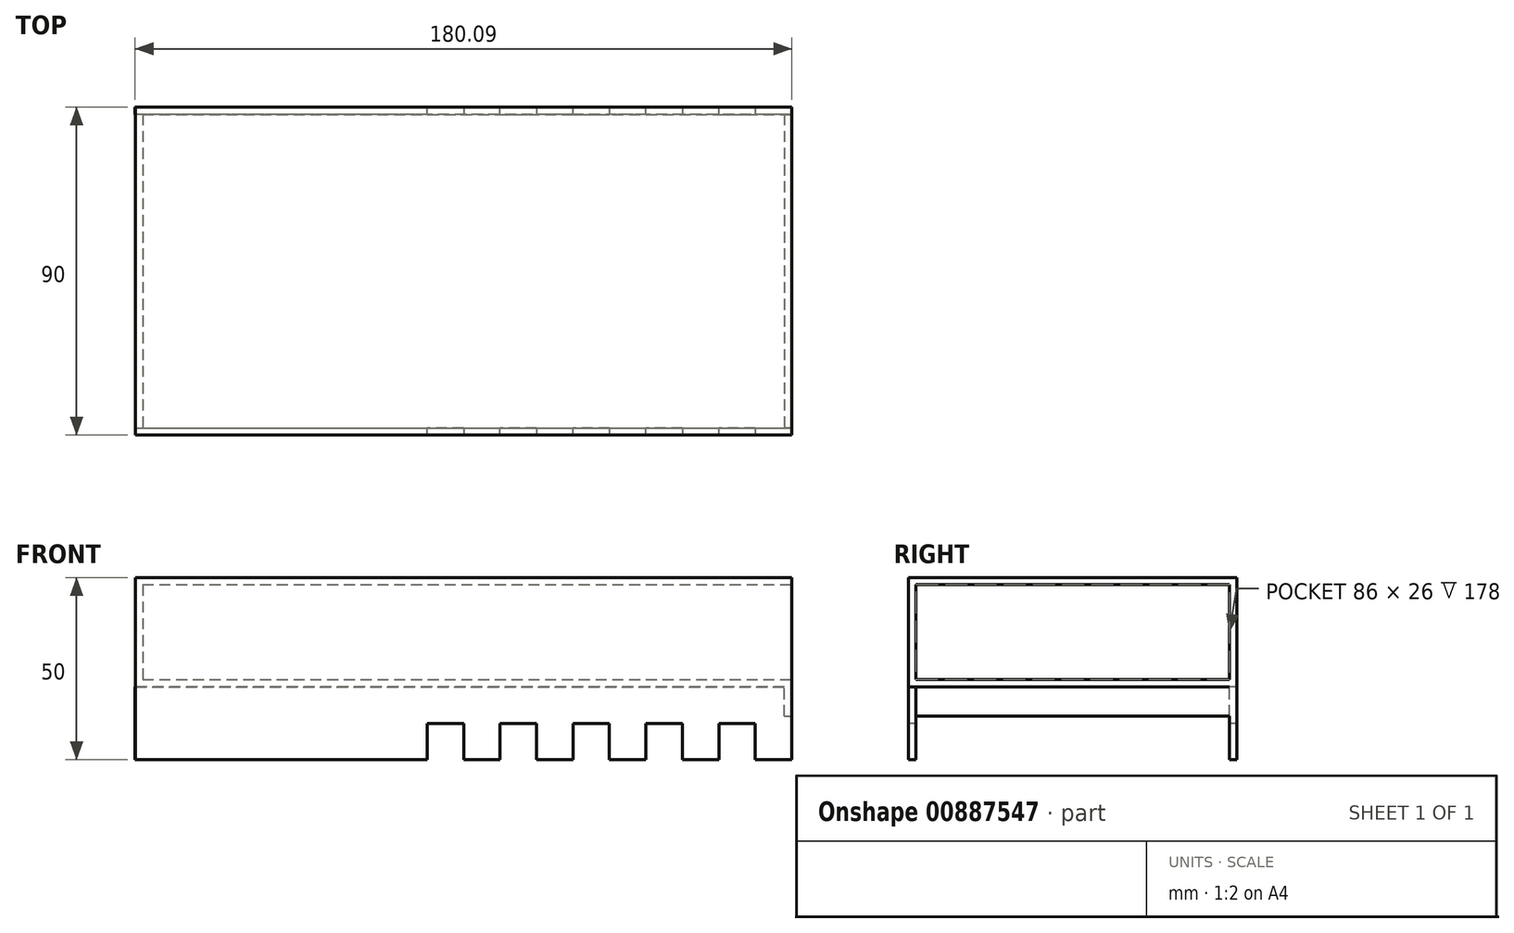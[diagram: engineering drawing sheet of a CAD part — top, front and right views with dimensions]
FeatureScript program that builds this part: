
annotation { "Feature Type Name" : "Feature", "Feature Type Description" : "" }
export const myFeature = defineFeature(function(context is Context, id is Id, definition is map)
    precondition{}
    {
        {
            var Q0;
            Q0=qCreatedBy(makeId("Top.planeOp"),FACE);
            var sketch = newSketch(context, id + "F0", { "sketchPlane" : qUnion([Q0])});
            skLineSegment(sketch, "E0.bottom", {"start": v(-90, 45) * mm, "end": v(90, 45) * mm});
            skLineSegment(sketch, "E0.top", {"start": v(-90, -45) * mm, "end": v(90, -45) * mm});
            skLineSegment(sketch, "E0.left", {"start": v(-90, 45) * mm, "end": v(-90, -45) * mm});
            skLineSegment(sketch, "E0.right", {"start": v(90, 45) * mm, "end": v(90, -45) * mm});
            skPoint(sketch, "E0.middle", {"position": v(0, 0) * mm});
            skSolve(sketch);
        }
        {
            var Q0;
            Q0=makeQuery(id+"F0.imprint","IMPRINT",FACE,{"disambiguationData":[TD([[makeQuery(id+"F0.imprint","IMPRINT",EDGE,{"derivedFrom":sQuery(id+"F0.wireOp",EDGE,"E0.bottom")}),-1.0]])]});
            extrude(context, id + "F1", {"entities" : qUnion([Q0]), "depth" : 30 * mm, "offsetDistance" : 25 * mm});
        }
        {
            var Q0;
            Q0=makeQuery(id+"F1.opExtrude","SWEPT_FACE",FACE,{"disambiguationData":[OSD([sQuery(id+"F0.wireOp",EDGE,"E0.right")])]});
            shell(context, id + "F2", {"entities" : qUnion([Q0]), "thickness" : 2 * mm});
        }
        {
            var Q0;
            Q0=qCreatedBy(makeId("Top.planeOp"),FACE);
            var sketch = newSketch(context, id + "F3", { "sketchPlane" : qUnion([Q0])});
            skLineSegment(sketch, "E1.bottom", {"start": v(90, 45) * mm, "end": v(-90.09, 45) * mm});
            skLineSegment(sketch, "E1.top", {"start": v(90, 43) * mm, "end": v(-90.09, 43) * mm});
            skLineSegment(sketch, "E1.left", {"start": v(90, 45) * mm, "end": v(90, 43) * mm});
            skLineSegment(sketch, "E1.right", {"start": v(-90.09, 45) * mm, "end": v(-90.09, 43) * mm});
            skLineSegment(sketch, "E2.top", {"start": v(90, -45) * mm, "end": v(-90, -45) * mm});
            skLineSegment(sketch, "E3", {"start": v(-90, -45) * mm, "end": v(-90, -43) * mm});
            skLineSegment(sketch, "E4", {"start": v(-90, -43) * mm, "end": v(90, -43) * mm});
            skLineSegment(sketch, "E5", {"start": v(90, -43) * mm, "end": v(90, -45) * mm});
            skSolve(sketch);
        }
        {
            var Q0;
            Q0=makeQuery(id+"F3.imprint","IMPRINT",FACE,{"disambiguationData":[TD([[makeQuery(id+"F3.imprint","IMPRINT",EDGE,{"derivedFrom":sQuery(id+"F3.wireOp",EDGE,"E1.bottom")}),1.0]])]});
            extrude(context, id + "F4", {"entities" : qUnion([Q0]), "operationType" : NewBodyOperationType.ADD, "oppositeDirection" : true, "depth" : 20 * mm, "offsetDistance" : 25 * mm});
        }
        {
            var Q0;
            Q0=qSketchRegion(id+"F3",true);
            extrude(context, id + "F5", {"entities" : qUnion([Q0]), "operationType" : NewBodyOperationType.ADD, "oppositeDirection" : true, "depth" : 20 * mm, "offsetDistance" : 25 * mm});
        }
        {
            var Q0;
            Q0=makeQuery(id+"F1.opExtrude","SWEPT_FACE",FACE,{"disambiguationData":[OSD([sQuery(id+"F0.wireOp",EDGE,"E0.top")])]});
            var sketch = newSketch(context, id + "F6", { "sketchPlane" : qUnion([Q0])});
            skLineSegment(sketch, "E6", {"start": v(103.9, -10) * mm, "end": v(-23.96, -10) * mm});
            skLineSegment(sketch, "E7", {"start": v(-23.96, -10) * mm, "end": v(-23.96, -20) * mm});
            skLineSegment(sketch, "E8", {"start": v(103.9, -10) * mm, "end": v(103.9, -20) * mm});
            skLineSegment(sketch, "E9", {"start": v(80, -10) * mm, "end": v(80, -20.06) * mm});
            skLineSegment(sketch, "E10", {"start": v(70, -10) * mm, "end": v(70, -20.02) * mm});
            skLineSegment(sketch, "E11", {"start": v(60, -10) * mm, "end": v(60, -20.06) * mm});
            skLineSegment(sketch, "E12", {"start": v(90, -20) * mm, "end": v(-23.96, -20) * mm});
            skLineSegment(sketch, "E13", {"start": v(50, -10) * mm, "end": v(50, -20) * mm});
            skLineSegment(sketch, "E14", {"start": v(40, -10) * mm, "end": v(40, -20) * mm});
            skLineSegment(sketch, "E15", {"start": v(30, -10) * mm, "end": v(30, -20) * mm});
            skLineSegment(sketch, "E16", {"start": v(20, -10) * mm, "end": v(20, -20) * mm});
            skLineSegment(sketch, "E17", {"start": v(10, -10) * mm, "end": v(10, -20) * mm});
            skLineSegment(sketch, "E18", {"start": v(0, -10) * mm, "end": v(0, -20) * mm});
            skLineSegment(sketch, "E19", {"start": v(-10, -10) * mm, "end": v(-10, -20) * mm});
            skSolve(sketch);
        }
        {
            var Q0;
            {var subQ0=sQuery(id+"F6.wireOp",EDGE,"E9");var subQ1=sQuery(id+"F6.wireOp",EDGE,"E6");var subQ2=makeQuery(id+"F6.imprint","INTERSECT",VERTEX,{"derivedFrom":[subQ1,subQ0]});Q0=makeQuery(id+"F6.imprint","IMPRINT",FACE,{"disambiguationData":[TD([[makeQuery(id+"F6.imprint","IMPRINT",EDGE,{"disambiguationData":[TD([[subQ2,-1.0]])],"derivedFrom":subQ1}),1.0]])]});}
            var Q1;
            {var subQ3=sQuery(id+"F6.wireOp",EDGE,"E13");Q1=makeQuery(id+"F6.imprint","IMPRINT",FACE,{"disambiguationData":[TD([[makeQuery(id+"F6.imprint","IMPRINT",EDGE,{"derivedFrom":subQ3}),1.0]])]});}
            var Q2;
            {var subQ0=sQuery(id+"F6.wireOp",EDGE,"E14");Q2=makeQuery(id+"F6.imprint","IMPRINT",FACE,{"disambiguationData":[TD([[makeQuery(id+"F6.imprint","IMPRINT",EDGE,{"derivedFrom":subQ0}),-1.0]])]});}
            var Q3;
            {var subQ0=sQuery(id+"F6.wireOp",EDGE,"E16");Q3=makeQuery(id+"F6.imprint","IMPRINT",FACE,{"disambiguationData":[TD([[makeQuery(id+"F6.imprint","IMPRINT",EDGE,{"derivedFrom":subQ0}),-1.0]])]});}
            var Q4;
            {var subQ0=sQuery(id+"F6.wireOp",EDGE,"E18");Q4=makeQuery(id+"F6.imprint","IMPRINT",FACE,{"disambiguationData":[TD([[makeQuery(id+"F6.imprint","IMPRINT",EDGE,{"derivedFrom":subQ0}),-1.0]])]});}
            extrude(context, id + "F7", {"entities" : qUnion([Q0, Q1, Q2, Q3, Q4]), "operationType" : NewBodyOperationType.REMOVE, "oppositeDirection" : true, "depth" : 100 * mm, "offsetDistance" : 25 * mm});
        }
        {
            var Q0;
            Q0=makeQuery(id+"F4.opExtrude","SWEPT_FACE",FACE,{"disambiguationData":[OSD([sQuery(id+"F3.wireOp",EDGE,"E1.left")])]});
            var sketch = newSketch(context, id + "F8", { "sketchPlane" : qUnion([Q0])});
            skLineSegment(sketch, "E20.bottom", {"start": v(45, 0) * mm, "end": v(-45, 0) * mm});
            skLineSegment(sketch, "E20.top", {"start": v(45, 0) * mm, "end": v(-45, 0) * mm});
            skLineSegment(sketch, "E20.left", {"start": v(45, 0) * mm, "end": v(45, 0) * mm});
            skLineSegment(sketch, "E20.right", {"start": v(-45, 0) * mm, "end": v(-45, 0) * mm});
            skLineSegment(sketch, "E21.top", {"start": v(45, -8) * mm, "end": v(-45, -8) * mm});
            skLineSegment(sketch, "E21.left", {"start": v(45, 0) * mm, "end": v(45, -8) * mm});
            skLineSegment(sketch, "E21.right", {"start": v(-45, 0) * mm, "end": v(-45, -8) * mm});
            skSolve(sketch);
        }
        {
            var Q0;
            {var subQ3=sQuery(id+"F8.wireOp",EDGE,"E21.right");Q0=makeQuery(id+"F8.imprint","IMPRINT",FACE,{"disambiguationData":[TD([[makeQuery(id+"F8.imprint","IMPRINT",EDGE,{"derivedFrom":subQ3}),1.0]])]});}
            var Q1;
            Q1=sQuery(id+"F8.wireOp",EDGE,"E21.top");
            extrude(context, id + "F9", {"entities" : qUnion([Q0]), "operationType" : NewBodyOperationType.ADD, "surfaceEntities" : qUnion([Q1]), "oppositeDirection" : true, "depth" : 2 * mm, "offsetDistance" : 25 * mm});
        }
    });
